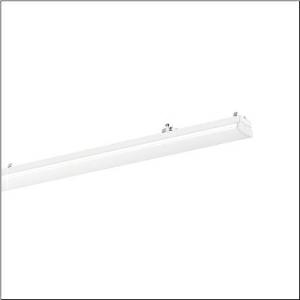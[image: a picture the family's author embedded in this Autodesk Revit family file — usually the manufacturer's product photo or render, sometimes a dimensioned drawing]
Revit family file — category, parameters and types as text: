
# Revit family: licross_11_recessed_opal_ho_51te1dmn4d5m
name_source: partatom
category: Lighting Fixtures
units: mm (PartAtom-declared; Revit-internal decimal feet)

## family parameters
Cut with Voids When Loaded = No
Host = Face
Light Source = No
Part Type = Normal
Room Calculation Point = No
Round Connector Dimension = Use Diameter
Shared = No

## types (1)
- --- (1 x LED, 13690 lm, 74.5 W, 4000K)
    Apparent Load = 75 VA
    CIE Flux Codes = 44 73 91 87 100
    Color Rendering = 80
    Color Temperature = 4000K
    Default Elevation = 1800 mm
    Description = Licross 11 recessed opal HO, luminaire insert, of sheet steel, coil coated, white, length: 1.500mm, width: 76mm, height: 87mm, LED rated luminous flux: 13.690lm, light colour: 840, SDCM (Standard Deviation of Colour Matching)MacAdam ≤ 2 SDCM (initial), control gear: ON/OFF Multilumen, with plug, 3-pole, with phase selection, mains connection: 220..240V, AC, 50/60Hz, rated input power: 75W, internal wiring halogen-free, primary optical cover: cover, of PMMA, light emission: direct with ceiling illumination distribution, primary light characteristic: symmetric, protection rating (complete): IP54, insulation class (complete): insulation class I (protective earthing), certification: CE, ENEC, VDE, UKCA, protection symbol: D if used in an environment with non-conductive dust loads with corresponding accessories, impact resistance: IK06, permissible ambient temperature for indoor applications: -35..+35°C, corresponds to IFS (International Featured Standards) requirements for safety and quality in the food industry, reducing of maximum allowable ambient temperature of 5°C with ceiling mounting, The light source and the operating device comply with the requirements of the Ecodesign Regulation (EU) 2019/2020 and are replaceable in accordance with this regulation, packaging unit: 1 piece
    Height = 83 mm
    Lamp = 1 x LED
    Lamp Light Flux = 13690 lm
    Lamp Power = 74.5 W
    Lamp count = 1
    Length = 1500 mm
    Luminous efficacy = 184 lm/W
    Manufacturer = Siteco
    ModVariant = No
    Model = 51TE1DMN4D5M
    Mounting Place = Ceiling
    Mounting Type = Pendant
    Number of Poles = 1
    OnlyDefault = Yes
    Power Factor = 1
    Product Name = Licross 11 recessed opal HO
    Product group = luminaire insert | ceiling pendant
    ProductGroupID = 901
    Protection Class = Protection class I
    Protection Degree = IP 54
    RLX_Detail_Level = 1
    RLX_Emergency_Light_Flux = 0 lm
    RLX_Emergency_Type = 0
    RLX_Emergency_Type_DB = No
    RlxData = <blob elided: 25137 chars, md5=53f5c163>
    Socket = socket
    Standby Power = 0 W
    System Light Flux = 13690 lm
    System Power = 75 W
    Type Comments = factory setting: luminous flux: 100 % | (A | C | E) | 174 mA
    Type Image = l_1313666.jpg
    URL = http://relux.com
    VarID = @adj_083513
    Voltage = 0 V
    Weight = 0.00 kg
    Width = 76 mm

## geometry (parser evidence)
native form markers: Blend x4, Sweep x15
no freeform markers — native parametric forms only
